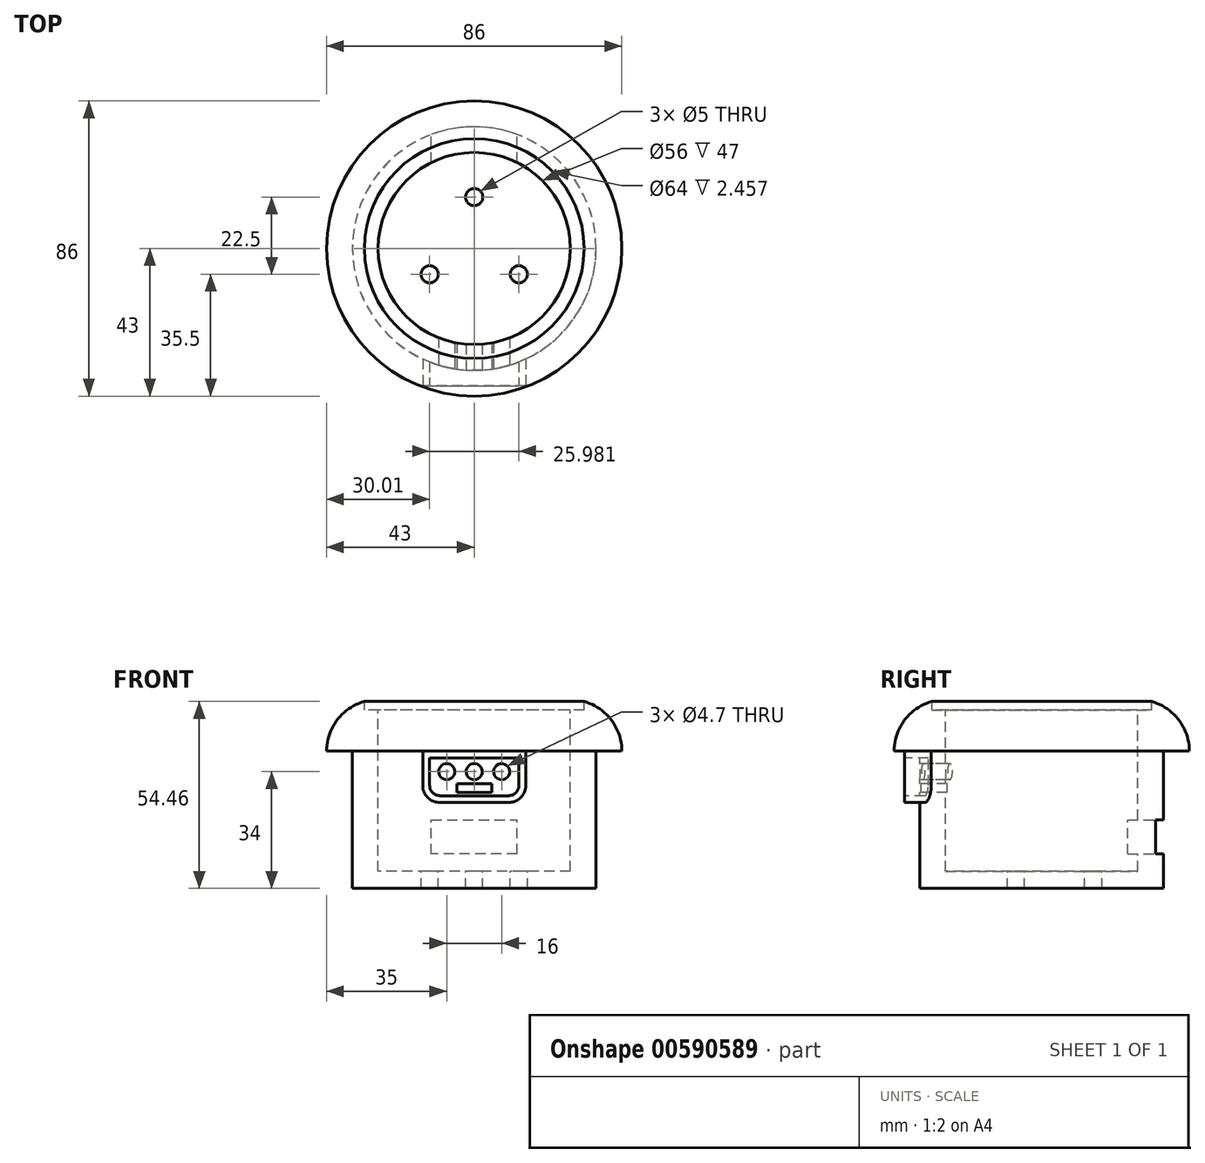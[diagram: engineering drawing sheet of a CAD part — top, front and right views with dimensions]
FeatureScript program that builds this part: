
annotation { "Feature Type Name" : "Feature", "Feature Type Description" : "" }
export const myFeature = defineFeature(function(context is Context, id is Id, definition is map)
    precondition{}
    {
        {
            var Q0;
            Q0=qCreatedBy(makeId("Front.planeOp"),FACE);
            var sketch = newSketch(context, id + "F0", { "sketchPlane" : qUnion([Q0])});
            skLineSegment(sketch, "E0", {"start": v(43, 30) * mm, "end": v(43, 15) * mm});
            skLineSegment(sketch, "E1", {"start": v(43, 15) * mm, "end": v(35.5, 15) * mm});
            skLineSegment(sketch, "E2", {"start": v(35.5, 15) * mm, "end": v(35.5, -15) * mm});
            skLineSegment(sketch, "E3", {"start": v(43, 30) * mm, "end": v(28, 30) * mm});
            skLineSegment(sketch, "E4", {"start": v(28, 30) * mm, "end": v(28, -20) * mm});
            skLineSegment(sketch, "E5", {"start": v(28, -20) * mm, "end": v(0, -20) * mm});
            skLineSegment(sketch, "E6", {"start": v(0, -25) * mm, "end": v(35.5, -25) * mm});
            skLineSegment(sketch, "E7", {"start": v(35.5, -25) * mm, "end": v(35.5, -15) * mm});
            skLineSegment(sketch, "E8", {"start": v(0, -20) * mm, "end": v(0, -25) * mm});
            skSolve(sketch);
        }
        {
            var Q0;
            Q0=makeQuery(id+"F0.imprint","IMPRINT",FACE,{"disambiguationData":[TD([[makeQuery(id+"F0.imprint","IMPRINT",EDGE,{"derivedFrom":sQuery(id+"F0.wireOp",EDGE,"E0")}),-1.0]])]});
            var Q1;
            Q1=sQuery(id+"F0.wireOp",EDGE,"E8");
            revolve(context, id + "F1", {"entities" : qUnion([Q0]), "axis" : qUnion([Q1]), "revolveType" : RevolveType.FULL});
        }
        {
            var Q0;
            Q0=makeQuery(id+"F1.opRevolve","SWEPT_EDGE",EDGE,{"disambiguationData":[OSD([sQuery(id+"F0.wireOp",EDGE,"E0"),sQuery(id+"F0.wireOp",EDGE,"E3")])]});
            fillet(context, id + "F2", {"entities" : qUnion([Q0]), "radius" : 15 * mm, "tangentPropagation" : true, "allowEdgeOverflow" : false});
        }
        {
            var Q0;
            Q0=makeQuery(id+"F1.opRevolve","SWEPT_FACE",FACE,{"disambiguationData":[OSD([sQuery(id+"F0.wireOp",EDGE,"E5")])]});
            var sketch = newSketch(context, id + "F3", { "sketchPlane" : qUnion([Q0])});
            skPoint(sketch, "E9", {"position": v(0, 15) * mm});
            skPoint(sketch, "E10.1.0", {"position": v(-13, -7.5) * mm});
            skPoint(sketch, "E10.2.0", {"position": v(13, -7.5) * mm});
            skPoint(sketch, "E10.center", {"position": v(0, 0) * mm});
            skSolve(sketch);
        }
        {
            var Q0;
            Q0=sQuery(id+"F3.wireOp",VERTEX,"E9");
            var Q1;
            Q1=sQuery(id+"F3.wireOp",VERTEX,"E10.1.0");
            var Q2;
            Q2=sQuery(id+"F3.wireOp",VERTEX,"E10.2.0");
            var Q3;
            Q3=makeQuery(id+"F1.opRevolve","SWEPT_BODY",BODY,{"disambiguationData":[OSD([sQuery(id+"F0.wireOp",EDGE,"E0"),sQuery(id+"F0.wireOp",EDGE,"E1"),sQuery(id+"F0.wireOp",EDGE,"E2"),sQuery(id+"F0.wireOp",EDGE,"E3"),sQuery(id+"F0.wireOp",EDGE,"E4"),sQuery(id+"F0.wireOp",EDGE,"E5"),sQuery(id+"F0.wireOp",EDGE,"E6"),sQuery(id+"F0.wireOp",EDGE,"E7"),sQuery(id+"F0.wireOp",EDGE,"E8")])]});
            hole(context, id + "F4", {"style" : HoleStyle.SIMPLE, "endStyle" : HoleEndStyle.THROUGH, "holeDiameter" : 5 * mm, "majorDiameter" : 5 * mm, "isTappedThrough" : true, "tappedDepth" : 12 * mm, "tapClearance" : 3, "locations" : qUnion([Q0, Q1, Q2]), "scope" : qUnion([Q3])});
        }
        {
            var Q0;
            Q0=qCreatedBy(makeId("Top.planeOp"),FACE);
            cPlane(context, id + "F5", {"entities" : qUnion([Q0]), "cplaneType" : CPlaneType.OFFSET, "offset" : 30 * mm, "width" : 150 * mm, "height" : 150 * mm});
        }
        {
            var Q0;
            Q0=qCreatedBy(id+"F5.planeOp",FACE);
            var sketch = newSketch(context, id + "F6", { "sketchPlane" : qUnion([Q0])});
            skLineSegment(sketch, "E11", {"start": v(0, 0) * mm, "end": v(32, 0) * mm});
            skCircle(sketch, "E12", {"center": v(0, 0) * mm, "radius": 32 * mm});
            skSolve(sketch);
        }
        {
            var Q0;
            Q0=makeQuery(id+"F6.imprint","IMPRINT",FACE,{"disambiguationData":[TD([[makeQuery(id+"F6.imprint","IMPRINT",EDGE,{"derivedFrom":sQuery(id+"F6.wireOp",EDGE,"E12")}),1.0]])]});
            extrude(context, id + "F7", {"entities" : qUnion([Q0]), "operationType" : NewBodyOperationType.REMOVE, "oppositeDirection" : true, "depth" : 3 * mm, "offsetDistance" : 25 * mm});
        }
        {
            var Q0;
            Q0=makeQuery(id+"F7.boolean.opBoolean","COPY",FACE,{"derivedFrom":makeQuery(id+"F7.opExtrude","CAP_FACE",FACE,{"disambiguationData":[OSD([sQuery(id+"F0.wireOp",EDGE,"E3"),sQuery(id+"F0.wireOp",EDGE,"E4"),sQuery(id+"F6.wireOp",EDGE,"E12")])],"isStart":false})});
            var sketch = newSketch(context, id + "F8", { "sketchPlane" : qUnion([Q0])});
            skPoint(sketch, "E13", {"position": v(0, 0) * mm});
            skSolve(sketch);
        }
        {
            var Q0;
            Q0=qCreatedBy(makeId("Front.planeOp"),FACE);
            cPlane(context, id + "F9", {"entities" : qUnion([Q0]), "cplaneType" : CPlaneType.OFFSET, "offset" : 40 * mm, "width" : 150 * mm, "height" : 150 * mm});
        }
        {
            var Q0;
            Q0=qCreatedBy(id+"F9.planeOp",FACE);
            var sketch = newSketch(context, id + "F10", { "sketchPlane" : qUnion([Q0])});
            skLineSegment(sketch, "E14", {"start": v(0, 0) * mm, "end": v(15, 0) * mm});
            skLineSegment(sketch, "E15", {"start": v(15, 0) * mm, "end": v(15, 15) * mm});
            skLineSegment(sketch, "E16", {"start": v(15, 15) * mm, "end": v(-15, 15) * mm});
            skLineSegment(sketch, "E17", {"start": v(-15, 15) * mm, "end": v(-15, 0) * mm});
            skLineSegment(sketch, "E18", {"start": v(-15, 0) * mm, "end": v(0, 0) * mm});
            skLineSegment(sketch, "E19", {"start": v(0, 0) * mm, "end": v(0, 2) * mm});
            skLineSegment(sketch, "E20", {"start": v(0, 2) * mm, "end": v(-13, 2) * mm});
            skLineSegment(sketch, "E21", {"start": v(-13, 2) * mm, "end": v(-13, 13) * mm});
            skLineSegment(sketch, "E22", {"start": v(-13, 13) * mm, "end": v(13, 13) * mm});
            skLineSegment(sketch, "E23", {"start": v(13, 13) * mm, "end": v(13, 2) * mm});
            skLineSegment(sketch, "E24", {"start": v(13, 2) * mm, "end": v(0, 2) * mm});
            skLineSegment(sketch, "E25", {"start": v(0, 2) * mm, "end": v(0, 5) * mm});
            skLineSegment(sketch, "E26", {"start": v(0, 5) * mm, "end": v(0, 9) * mm});
            skLineSegment(sketch, "E27", {"start": v(0, 9) * mm, "end": v(8, 9) * mm});
            skLineSegment(sketch, "E28", {"start": v(8, 9) * mm, "end": v(0, 9) * mm});
            skLineSegment(sketch, "E29", {"start": v(0, 9) * mm, "end": v(-8, 9) * mm});
            skSolve(sketch);
        }
        {
            var Q0;
            Q0 = qSketchRegion(id + "F10", true);
            extrude(context, id + "F11", {"entities" : qUnion([Q0]), "operationType" : NewBodyOperationType.ADD, "oppositeDirection" : true, "depth" : 25 * mm, "offsetDistance" : 25 * mm});
        }
        {
            var Q0;
            Q0=makeQuery(id+"F8.imprint","IMPRINT",FACE,{"disambiguationData":[TD([[makeQuery(id+"F8.imprint","IMPRINT",EDGE,{"derivedFrom":makeQuery(id+"F7.boolean.opBoolean","INTERSECT",EDGE,{"derivedFrom":[makeQuery(id+"F1.opRevolve","SWEPT_FACE",FACE,{"disambiguationData":[OSD([sQuery(id+"F0.wireOp",EDGE,"E4")])]}),makeQuery(id+"F7.opExtrude","CAP_FACE",FACE,{"disambiguationData":[OSD([sQuery(id+"F6.wireOp",EDGE,"E12")])],"isStart":false})]})}),-1.0]])]});
            extrude(context, id + "F12", {"entities" : qUnion([Q0]), "operationType" : NewBodyOperationType.REMOVE, "oppositeDirection" : true, "depth" : 40 * mm, "offsetDistance" : 25 * mm});
        }
        {
            var Q0;
            {var subQ0=sQuery(id+"F10.wireOp",EDGE,"E18");var subQ1=sQuery(id+"F10.wireOp",EDGE,"E17");Q0=makeQuery(id+"F11.boolean.opBoolean","SPLIT",EDGE,{"disambiguationData":[TD([makeQuery(id+"F1.opRevolve","SWEPT_FACE",FACE,{"disambiguationData":[OSD([sQuery(id+"F0.wireOp",EDGE,"E2"),sQuery(id+"F0.wireOp",EDGE,"E7")])]})])],"derivedFrom":makeQuery(id+"F11.opExtrude","SWEPT_EDGE",EDGE,{"disambiguationData":[OSD([subQ1,subQ0])]})});}
            var Q1;
            {var subQ1=sQuery(id+"F10.wireOp",EDGE,"E15");var subQ2=sQuery(id+"F10.wireOp",EDGE,"E14");Q1=makeQuery(id+"F11.boolean.opBoolean","SPLIT",EDGE,{"disambiguationData":[TD([makeQuery(id+"F1.opRevolve","SWEPT_FACE",FACE,{"disambiguationData":[OSD([sQuery(id+"F0.wireOp",EDGE,"E2"),sQuery(id+"F0.wireOp",EDGE,"E7")])]})])],"derivedFrom":makeQuery(id+"F11.opExtrude","SWEPT_EDGE",EDGE,{"disambiguationData":[OSD([subQ2,subQ1])]})});}
            fillet(context, id + "F13", {"entities" : qUnion([Q0, Q1]), "radius" : 5 * mm, "tangentPropagation" : true, "allowEdgeOverflow" : false});
        }
        {
            var Q0;
            {var subQ1=sQuery(id+"F10.wireOp",EDGE,"E21");var subQ2=sQuery(id+"F10.wireOp",EDGE,"E20");Q0=makeQuery(id+"F11.boolean.opBoolean","SPLIT",EDGE,{"disambiguationData":[TD([makeQuery(id+"F1.opRevolve","SWEPT_FACE",FACE,{"disambiguationData":[OSD([sQuery(id+"F0.wireOp",EDGE,"E2"),sQuery(id+"F0.wireOp",EDGE,"E7")])]})])],"derivedFrom":makeQuery(id+"F11.opExtrude","SWEPT_EDGE",EDGE,{"disambiguationData":[OSD([subQ2,subQ1])]})});}
            var Q1;
            {var subQ0=sQuery(id+"F10.wireOp",EDGE,"E23");var subQ1=sQuery(id+"F10.wireOp",EDGE,"E24");Q1=makeQuery(id+"F11.boolean.opBoolean","SPLIT",EDGE,{"disambiguationData":[TD([makeQuery(id+"F1.opRevolve","SWEPT_FACE",FACE,{"disambiguationData":[OSD([sQuery(id+"F0.wireOp",EDGE,"E2"),sQuery(id+"F0.wireOp",EDGE,"E7")])]})])],"derivedFrom":makeQuery(id+"F11.opExtrude","SWEPT_EDGE",EDGE,{"disambiguationData":[OSD([subQ0,subQ1])]})});}
            fillet(context, id + "F14", {"entities" : qUnion([Q0, Q1]), "radius" : 3 * mm, "tangentPropagation" : true, "allowEdgeOverflow" : false});
        }
        {
            var Q0;
            Q0=sQuery(id+"F10.wireOp",VERTEX,"E29.end");
            var Q1;
            Q1=sQuery(id+"F10.wireOp",VERTEX,"E28.end");
            var Q2;
            Q2=sQuery(id+"F10.wireOp",VERTEX,"E28.start");
            var Q3;
            Q3=makeQuery(id+"F1.opRevolve","SWEPT_BODY",BODY,{"disambiguationData":[OSD([sQuery(id+"F0.wireOp",EDGE,"E0"),sQuery(id+"F0.wireOp",EDGE,"E1"),sQuery(id+"F0.wireOp",EDGE,"E2"),sQuery(id+"F0.wireOp",EDGE,"E3"),sQuery(id+"F0.wireOp",EDGE,"E4"),sQuery(id+"F0.wireOp",EDGE,"E5"),sQuery(id+"F0.wireOp",EDGE,"E6"),sQuery(id+"F0.wireOp",EDGE,"E7"),sQuery(id+"F0.wireOp",EDGE,"E8")])]});
            hole(context, id + "F15", {"style" : HoleStyle.SIMPLE, "endStyle" : HoleEndStyle.BLIND, "holeDiameter" : 4.7 * mm, "majorDiameter" : 5 * mm, "holeDepth" : 12 * mm, "isTappedThrough" : true, "tappedDepth" : 12 * mm, "tapClearance" : 3, "locations" : qUnion([Q0, Q1, Q2]), "scope" : qUnion([Q3])});
        }
        {
            var Q0;
            Q0=qCreatedBy(makeId("Front.planeOp"),FACE);
            cPlane(context, id + "F16", {"entities" : qUnion([Q0]), "cplaneType" : CPlaneType.OFFSET, "offset" : 36 * mm, "oppositeDirection" : true, "width" : 150 * mm, "height" : 150 * mm});
        }
        {
            var Q0;
            Q0=qCreatedBy(id+"F16.planeOp",FACE);
            var sketch = newSketch(context, id + "F17", { "sketchPlane" : qUnion([Q0])});
            skLineSegment(sketch, "E30", {"start": v(0, 0) * mm, "end": v(0, -15) * mm});
            skLineSegment(sketch, "E31", {"start": v(0, -15) * mm, "end": v(12.5, -15) * mm});
            skLineSegment(sketch, "E32.bottom", {"start": v(12.5, -15) * mm, "end": v(-12.5, -15) * mm});
            skLineSegment(sketch, "E32.top", {"start": v(12.5, -5) * mm, "end": v(-12.5, -5) * mm});
            skLineSegment(sketch, "E32.left", {"start": v(12.5, -15) * mm, "end": v(12.5, -5) * mm});
            skLineSegment(sketch, "E32.right", {"start": v(-12.5, -15) * mm, "end": v(-12.5, -5) * mm});
            skSolve(sketch);
        }
        {
            var Q0;
            {var subQ5=sQuery(id+"F17.wireOp",EDGE,"E32.left");Q0=makeQuery(id+"F17.imprint","IMPRINT",FACE,{"disambiguationData":[TD([[makeQuery(id+"F17.imprint","IMPRINT",EDGE,{"derivedFrom":subQ5}),1.0]])]});}
            var Q1;
            {var subQ5=sQuery(id+"F17.wireOp",EDGE,"E32.right");Q1=makeQuery(id+"F17.imprint","IMPRINT",FACE,{"disambiguationData":[TD([[makeQuery(id+"F17.imprint","IMPRINT",EDGE,{"derivedFrom":subQ5}),-1.0]])]});}
            extrude(context, id + "F18", {"entities" : qUnion([Q0, Q1]), "operationType" : NewBodyOperationType.REMOVE, "depth" : 25 * mm, "offsetDistance" : 25 * mm});
        }
        {
            var Q0;
            Q0=makeQuery(id+"F10.imprint","IMPRINT",FACE,{"disambiguationData":[TD([[makeQuery(id+"F10.imprint","IMPRINT",EDGE,{"derivedFrom":sQuery(id+"F10.wireOp",EDGE,"E14")}),1.0]])]});
            var sketch = newSketch(context, id + "F19", { "sketchPlane" : qUnion([Q0])});
            skLineSegment(sketch, "E33", {"start": v(0, 0) * mm, "end": v(0, 3) * mm});
            skLineSegment(sketch, "E34", {"start": v(0, 3) * mm, "end": v(5.1, 3) * mm});
            skLineSegment(sketch, "E35", {"start": v(5.1, 3) * mm, "end": v(5.1, 5.54) * mm});
            skLineSegment(sketch, "E36", {"start": v(5.1, 5.54) * mm, "end": v(-5.1, 5.54) * mm});
            skLineSegment(sketch, "E37", {"start": v(-5.1, 5.54) * mm, "end": v(-5.1, 3) * mm});
            skLineSegment(sketch, "E38", {"start": v(-5.1, 3) * mm, "end": v(0, 3) * mm});
            skSolve(sketch);
        }
        {
            var Q0;
            Q0 = qSketchRegion(id + "F19", true);
            extrude(context, id + "F20", {"entities" : qUnion([Q0]), "operationType" : NewBodyOperationType.REMOVE, "oppositeDirection" : true, "depth" : 25 * mm, "offsetDistance" : 25 * mm});
        }
    });
